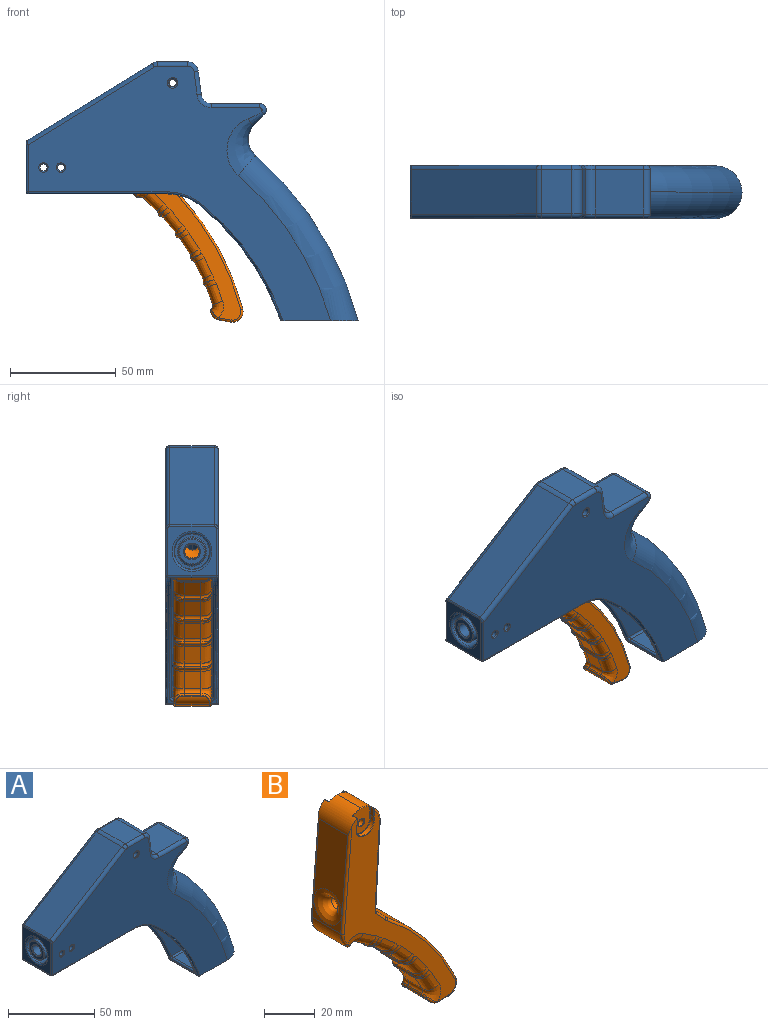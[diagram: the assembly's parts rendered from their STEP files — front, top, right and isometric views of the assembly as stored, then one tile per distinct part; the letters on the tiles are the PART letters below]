
ASSEMBLY  parts=2 mates=1
PART A: 167 faces, bbox 174.9x30.6x133.7 mm
  f0: cylinder r=3.5mm len=44.85mm, axis (-1,0,0), area 930.7mm2, adj f96,f97,f103,f104,f111,f113
  f1: cone r=6.35mm half-angle=0.3deg, axis (1,0,0), area 902mm2, adj f98,f99,f105,f106,f112,f114
  f2: cone r=8.3mm half-angle=0.3deg, axis (-1,0,0), area 1204.9mm2, adj f48,f70,f100,f101,f107,f108
  f3: plane 114.93x97.12mm, normal (0,1,0), area 3888.3mm2, adj f67,f68,f69,f80,f123,f129,f132,f136
  f4: plane 17.5x9.2mm, normal (0.52,0,-0.85), area 189.1mm2, adj f53,f140,f146,f149
  f5: plane 114.93x97.12mm, normal (0,-1,0), area 3888.3mm2, adj f64,f65,f66,f82,f115,f116,f120,f121
  f6: cylinder r=120mm len=53.62mm, axis (0,1,0), area 118.4mm2, adj f7,f15,f119,f121,f122,f126,f129,f161
  f7: cylinder r=25mm len=15.72mm, axis (0,1,0), area 12.8mm2, adj f6,f14,f125,f164
  f8: plane 21x11.13mm, normal (0.99,0,0.13), area 235.7mm2, adj f9,f21,f30,f43
  f9: cylinder r=5mm len=21mm, axis (0,1,0), area 151.3mm2, adj f8,f10,f29,f44
  f10: plane 21x14.2mm, normal (0,0,1), area 298.1mm2, adj f9,f11,f28,f45
  f11: cylinder r=5mm len=21mm, axis (0,1,0), area 58mm2, adj f10,f12,f27,f46
  f12: plane 59.18x36.47mm, normal (-0.52,0,0.85), area 1459.8mm2, adj f11,f26,f47,f75
  f13: plane 23.44x23mm, normal (-1,0,0), area 258.5mm2, adj f70,f71,f72,f73,f74,f75,f76
  f14: plane 65.73x23mm, normal (0,0,-1), area 1021.6mm2, adj f7,f15,f72,f128,f131,f135,f136,f139
  f15: cylinder r=25mm len=15.72mm, axis (0,1,0), area 12.8mm2, adj f6,f14,f132,f160
  f16: plane 37.37x26.55mm, normal (0,0,-1), area 826mm2, adj f22,f23,f36,f37,f161,f162,f163
  f17: cylinder r=10mm len=16.85mm, axis (0,1,0), area 138.3mm2, adj f18,f35,f38
  f18: plane 21.39x5.09mm, normal (0.71,0,-0.71), area 129.6mm2, adj f17,f19,f34,f39
  f19: cylinder r=3mm len=21mm, axis (0,1,0), area 148.4mm2, adj f18,f20,f33,f40
  f20: plane 22.76x21mm, normal (0,0,1), area 477.9mm2, adj f19,f21,f32,f41
  f21: cylinder r=5mm len=21mm, axis (0,1,0), area 151.3mm2, adj f8,f20,f31,f42
  f22: plane 143.42x120.75mm, normal (0,-1,0), area 5946.3mm2, adj f16,f37,f38,f39,f40,f41,f42,f43
  f23: plane 143.42x120.74mm, normal (0,1,0), area 5946.2mm2, adj f16,f26,f27,f28,f29,f30,f31,f32
  f24: cylinder r=2mm len=4.25mm, axis (0,-1,0), area 53.4mm2, adj f77,f84
  f25: cylinder r=2mm len=4.25mm, axis (0,1,0), area 53.4mm2, adj f78,f83
  f26: cylinder r=2mm len=60.75mm, axis (-0.85,0,-0.52), area 219.3mm2, adj f12,f23,f27,f73
  f27: torus R=3mm, axis (0,-1,0), area 7.4mm2, adj f11,f23,f26,f28
  f28: cylinder r=2mm len=14.2mm, axis (-1,0,0), area 44.6mm2, adj f10,f23,f27,f29
  f29: torus R=3mm, axis (0,-1,0), area 19.3mm2, adj f9,f23,f28,f30
  f30: cylinder r=2mm len=11.39mm, axis (-0.13,0,0.99), area 35.3mm2, adj f8,f23,f29,f31
  f31: torus R=7mm, axis (0,-1,0), area 25.9mm2, adj f21,f23,f30,f32
  f32: cylinder r=2mm len=22.76mm, axis (-1,0,0), area 71.5mm2, adj f20,f23,f31,f33
  f33: torus R=1mm, axis (0,-1,0), area 16.8mm2, adj f19,f23,f32,f34
  f34: bspline ~7.58x7.43mm, area 32.1mm2, adj f18,f23,f33,f35
  f35: bspline ~26.95x13.55mm, area 317.6mm2, adj f17,f23,f34,f36
  f36: torus R=142.5mm, axis (0,-1,0), area 1744.8mm2, adj f16,f23,f35,f37
  f37: torus R=142.5mm, axis (0,-1,0), area 1744.8mm2, adj f16,f22,f36,f38
  f38: bspline ~26.95x13.55mm, area 317.6mm2, adj f17,f22,f37,f39
  f39: bspline ~7.58x7.43mm, area 32.1mm2, adj f18,f22,f38,f40
  f40: torus R=1mm, axis (0,-1,0), area 16.8mm2, adj f19,f22,f39,f41
  f41: cylinder r=2mm len=22.76mm, axis (1,0,0), area 71.5mm2, adj f20,f22,f40,f42
  f42: torus R=7mm, axis (0,-1,0), area 25.9mm2, adj f21,f22,f41,f43
  f43: cylinder r=2mm len=11.39mm, axis (0.13,0,-0.99), area 35.3mm2, adj f8,f22,f42,f44
  f44: torus R=3mm, axis (0,-1,0), area 19.3mm2, adj f9,f22,f43,f45
  f45: cylinder r=2mm len=14.2mm, axis (1,0,0), area 44.6mm2, adj f10,f22,f44,f46
  f46: torus R=3mm, axis (0,-1,0), area 7.4mm2, adj f11,f22,f45,f47
  f47: cylinder r=2mm len=60.75mm, axis (0.85,0,0.52), area 219.3mm2, adj f12,f22,f46,f76
  f48: plane 16.6x16.6mm, normal (-1,0,0), area 62.6mm2, adj f2,f114
  f49: plane 11.71x11.71mm, normal (-1,0,0), area 57.4mm2, adj f112,f113
  f50: plane 17.5x11.13mm, normal (-0.99,0,-0.13), area 196.4mm2, adj f51,f59,f127,f153
  f51: cylinder r=2.25mm len=17.5mm, axis (0,1,0), area 56.7mm2, adj f50,f52,f130,f152
  f52: plane 17.5x14.2mm, normal (0,0,-1), area 248.4mm2, adj f51,f53,f133,f151
  f53: cylinder r=2.25mm len=17.5mm, axis (0,1,0), area 21.7mm2, adj f4,f52,f137,f150
  f54: plane 31.15x17.5mm, normal (0,0,1), area 510.8mm2, adj f116,f117,f122,f123
  f55: cylinder r=12.75mm len=18.65mm, axis (0,1,0), area 176.3mm2, adj f56,f65,f68
  f56: plane 17.54x4.74mm, normal (-0.71,0,0.71), area 116.1mm2, adj f55,f57,f64,f69,f115,f157
  f57: cylinder r=0.25mm len=17.5mm, axis (0,1,0), area 10.3mm2, adj f56,f58,f118,f156
  f58: plane 22.76x17.5mm, normal (0,0,-1), area 398.3mm2, adj f57,f59,f120,f155
  f59: cylinder r=7.75mm len=17.5mm, axis (0,1,0), area 195.4mm2, adj f50,f58,f124,f154
  f60: cylinder r=4.75mm len=9.5mm, axis (0,-1,0), area 44.8mm2, adj f80,f81
  f61: plane 8.5x8.5mm, normal (0,1,0), area 37.1mm2, adj f77,f81
  f62: cylinder r=4.75mm len=9.5mm, axis (0,1,0), area 44.8mm2, adj f79,f82
  f63: plane 8.5x8.5mm, normal (0,-1,0), area 37.1mm2, adj f78,f79
  f64: offset ~10.06x9.58mm, area 1.5mm2, adj f5,f56,f65,f115
  f65: offset ~32.45x19.05mm, area 253.4mm2, adj f5,f55,f64,f66
  f66: torus R=142.5mm, axis (0,-1,0), area 1277mm2, adj f5,f65,f67,f117
  f67: torus R=142.5mm, axis (0,-1,0), area 1277mm2, adj f3,f66,f68,f117
  f68: offset ~32.45x19.05mm, area 253.4mm2, adj f3,f55,f67,f69
  f69: offset ~10.06x9.58mm, area 1.5mm2, adj f3,f56,f68,f157
  f70: torus R=9.44mm, axis (1,0,0), area 86.6mm2, adj f2,f13
  f71: cylinder r=1mm len=22.27mm, axis (0,0,-1), area 35mm2, adj f13,f23,f73,f166
  f72: cylinder r=1mm len=23mm, axis (0,1,0), area 36.1mm2, adj f13,f14,f158,f166
  f73: bspline ~2.39x2.15mm, area 3.1mm2, adj f13,f26,f71,f75
  f74: cylinder r=1mm len=22.27mm, axis (0,0,1), area 35mm2, adj f13,f22,f76,f158
  f75: cylinder r=1mm len=21mm, axis (0,1,0), area 21.4mm2, adj f12,f13,f73,f76
  f76: bspline ~2.39x2.07mm, area 3.1mm2, adj f13,f47,f74,f75
  f77: torus R=2.5mm, axis (0,-1,0), area 10.8mm2, adj f24,f61
  f78: torus R=2.5mm, axis (0,1,0), area 10.8mm2, adj f25,f63
  f79: torus R=4.25mm, axis (0,1,0), area 22.5mm2, adj f62,f63
  f80: torus R=5.25mm, axis (0,-1,0), area 24.3mm2, adj f3,f60
  f81: torus R=4.25mm, axis (0,-1,0), area 22.5mm2, adj f60,f61
  f82: torus R=5.25mm, axis (0,-1,0), area 24.3mm2, adj f5,f62
  f83: torus R=2.5mm, axis (0,-1,0), area 10.8mm2, adj f23,f25
  f84: torus R=2.5mm, axis (0,-1,0), area 10.8mm2, adj f22,f24
  f85: plane 17.5x2.16mm, normal (1,0,0), area 37.8mm2, adj f141,f142,f146,f147
  f86: plane 49.74x17.5mm, normal (0.99,0,-0.13), area 827.3mm2, adj f111,f134,f135,f142,f143
  f87: cylinder r=1.7mm len=3.4mm, axis (0,1,0), area 35.9mm2, adj f108,f109
  f88: cylinder r=1.7mm len=3.4mm, axis (0,1,0), area 34.3mm2, adj f102,f107
  f89: cylinder r=1.7mm len=3.4mm, axis (0,1,0), area 35.3mm2, adj f101,f110
  f90: cylinder r=1.7mm len=3.4mm, axis (0,1,0), area 33.8mm2, adj f95,f100
  f91: cylinder r=1.7mm len=3.4mm, axis (0,1,0), area 24.3mm2, adj f104,f106
  f92: cylinder r=1.7mm len=3.4mm, axis (0,1,0), area 23mm2, adj f103,f105
  f93: cylinder r=1.7mm len=3.4mm, axis (0,1,0), area 23.7mm2, adj f97,f99
  f94: cylinder r=1.7mm len=3.4mm, axis (0,1,0), area 22.5mm2, adj f96,f98
  f95: torus R=2.2mm, axis (0,-1,0), area 9.3mm2, adj f22,f90
  f96: bspline ~4.41x3.85mm, area 7.5mm2, adj f0,f94
  f97: bspline ~4.41x3.85mm, area 7.5mm2, adj f0,f93
  f98: bspline ~4.77x4.41mm, area 10.7mm2, adj f1,f94
  f99: bspline ~4.78x4.4mm, area 10.7mm2, adj f1,f93
  f100: bspline ~4.41x4.16mm, area 8.5mm2, adj f2,f90
  f101: bspline ~4.41x4.16mm, area 8.5mm2, adj f2,f89
  f102: torus R=2.2mm, axis (0,-1,0), area 9.3mm2, adj f22,f88
  f103: bspline ~4.41x3.85mm, area 7.5mm2, adj f0,f92
  f104: bspline ~4.41x3.85mm, area 7.5mm2, adj f0,f91
  f105: bspline ~4.77x4.41mm, area 10.7mm2, adj f1,f92
  f106: bspline ~4.78x4.4mm, area 10.7mm2, adj f1,f91
  f107: bspline ~4.41x4.16mm, area 8.5mm2, adj f2,f88
  f108: bspline ~4.41x4.15mm, area 8.5mm2, adj f2,f87
  f109: torus R=2.2mm, axis (0,-1,0), area 9.3mm2, adj f23,f87
  f110: torus R=2.2mm, axis (0,-1,0), area 9.3mm2, adj f23,f89
  f111: bspline ~8x8mm, area 18.3mm2, adj f0,f86
  f112: torus R=5.85mm, axis (1,0,0), area 30.3mm2, adj f1,f49
  f113: torus R=4mm, axis (1,0,0), area 18.2mm2, adj f0,f49
  f114: torus R=7mm, axis (-1,0,0), area 32.8mm2, adj f1,f48
  f115: cylinder r=1mm len=4.92mm, axis (0.71,0,0.71), area 7.9mm2, adj f5,f56,f64,f118
  f116: cylinder r=1mm len=22.74mm, axis (-1,0,0), area 35.1mm2, adj f5,f54,f117,f119
  f117: bspline ~19.52x11.67mm, area 53mm2, adj f54,f66,f67,f116,f123
  f118: bspline ~2.41x1.31mm, area 0.5mm2, adj f57,f115,f120
  f119: bspline ~2.46x2.42mm, area 3.9mm2, adj f6,f116,f121,f122
  f120: cylinder r=1mm len=22.76mm, axis (1,0,0), area 34.3mm2, adj f5,f58,f118,f124
  f121: torus R=121mm, axis (0,-1,0), area 100.1mm2, adj f5,f6,f119,f125
  f122: cylinder r=1mm len=17.5mm, axis (0,1,0), area 33.5mm2, adj f6,f54,f119,f126
  f123: cylinder r=1mm len=22.74mm, axis (1,0,0), area 35.1mm2, adj f3,f54,f117,f126
  f124: torus R=8.75mm, axis (0,-1,0), area 18.4mm2, adj f5,f59,f120,f127
  f125: torus R=26mm, axis (0,-1,0), area 27.1mm2, adj f5,f7,f121,f128
  f126: bspline ~2.58x2.12mm, area 3.9mm2, adj f6,f122,f123,f129
  f127: cylinder r=1mm len=11.26mm, axis (0.13,0,-0.99), area 17.6mm2, adj f5,f50,f124,f130
  f128: cylinder r=1mm len=20.86mm, axis (1,0,0), area 32.8mm2, adj f5,f14,f125,f131
  f129: torus R=121mm, axis (0,-1,0), area 100.1mm2, adj f3,f6,f126,f132
  f130: torus R=1.25mm, axis (0,-1,0), area 4.3mm2, adj f5,f51,f127,f133
  f131: bspline ~2.51x2.02mm, area 3.3mm2, adj f14,f128,f134,f135
  f132: torus R=26mm, axis (0,-1,0), area 27.1mm2, adj f3,f15,f129,f136
  f133: cylinder r=1mm len=14.2mm, axis (1,0,0), area 22.3mm2, adj f5,f52,f130,f137
  f134: cylinder r=1mm len=49.87mm, axis (-0.13,0,-0.99), area 78.6mm2, adj f5,f86,f131,f138
  f135: cylinder r=1mm len=17.5mm, axis (0,-1,0), area 25.2mm2, adj f14,f86,f131,f139
  f136: cylinder r=1mm len=20.86mm, axis (-1,0,0), area 32.8mm2, adj f3,f14,f132,f139
  f137: torus R=1.25mm, axis (0,-1,0), area 1.6mm2, adj f5,f53,f133,f140
  f138: torus R=2mm, axis (0,-1,0), area 0.3mm2, adj f5,f134,f141,f142
  f139: bspline ~2.02x2mm, area 3.3mm2, adj f14,f135,f136,f143
  f140: cylinder r=1mm len=9.72mm, axis (0.85,0,0.52), area 17mm2, adj f4,f5,f137,f144
  f141: cylinder r=1mm len=2.16mm, axis (0,0,-1), area 3.4mm2, adj f5,f85,f138,f144
  f142: cylinder r=1mm len=17.5mm, axis (0,1,0), area 2.3mm2, adj f85,f86,f138,f145
  f143: cylinder r=1mm len=49.87mm, axis (-0.13,0,-0.99), area 78.6mm2, adj f3,f86,f139,f145
  f144: sphere r=1mm, area 0.7mm2, adj f140,f141,f146
  f145: torus R=2mm, axis (0,-1,0), area 0.3mm2, adj f3,f142,f143,f147
  f146: cylinder r=1mm len=17.5mm, axis (0,1,0), area 17.8mm2, adj f4,f85,f144,f148
  f147: cylinder r=1mm len=2.16mm, axis (0,0,1), area 3.4mm2, adj f3,f85,f145,f148
  f148: sphere r=1mm, area 0.7mm2, adj f146,f147,f149
  f149: cylinder r=1mm len=9.72mm, axis (0.85,0,0.52), area 17mm2, adj f3,f4,f148,f150
  f150: torus R=1.25mm, axis (0,-1,0), area 1.6mm2, adj f3,f53,f149,f151
  f151: cylinder r=1mm len=14.2mm, axis (1,0,0), area 22.3mm2, adj f3,f52,f150,f152
  f152: torus R=1.25mm, axis (0,-1,0), area 4.3mm2, adj f3,f51,f151,f153
  f153: cylinder r=1mm len=11.26mm, axis (0.13,0,-0.99), area 17.6mm2, adj f3,f50,f152,f154
  f154: torus R=8.75mm, axis (0,-1,0), area 18.4mm2, adj f3,f59,f153,f155
  f155: cylinder r=1mm len=22.76mm, axis (1,0,0), area 34.3mm2, adj f3,f58,f154,f156
  f156: bspline ~2.41x1.31mm, area 0.5mm2, adj f57,f155,f157
  f157: cylinder r=1mm len=4.92mm, axis (-0.71,0,-0.71), area 7.9mm2, adj f3,f56,f69,f156
  f158: sphere r=1mm, area 1.6mm2, adj f72,f74,f159
  f159: cylinder r=1mm len=65.73mm, axis (-1,0,0), area 103.2mm2, adj f14,f22,f158,f160
  f160: torus R=26mm, axis (0,-1,0), area 27.1mm2, adj f15,f22,f159,f161
  f161: torus R=121mm, axis (0,-1,0), area 105.6mm2, adj f6,f16,f22,f160,f162
  f162: cylinder r=1mm len=24.89mm, axis (0,1,0), area 29.5mm2, adj f6,f16,f161,f163
  f163: torus R=121mm, axis (0,-1,0), area 105.6mm2, adj f6,f16,f23,f162,f164
  f164: torus R=26mm, axis (0,-1,0), area 27.1mm2, adj f7,f23,f163,f165
  f165: cylinder r=1mm len=65.73mm, axis (1,0,0), area 103.2mm2, adj f14,f23,f164,f166
  f166: sphere r=1mm, area 2.1mm2, adj f71,f72,f165
PART B: 147 faces, bbox 74.2x18.1x114.9 mm
  f0: cylinder r=109.84mm len=12.17mm, axis (0,1,0), area 3.5mm2, adj f13,f72,f73,f74
  f1: cylinder r=9mm len=16mm, axis (0,1,0), area 216mm2, adj f2,f21,f79,f85,f119,f121,f122,f131
  f2: cylinder r=9mm len=18mm, axis (0,1,0), area 209.7mm2, adj f1,f12,f22,f23,f69,f77,f114,f115
  f3: cylinder r=1.65mm len=13.08mm, axis (0,1,0), area 135.6mm2, adj f137,f138
  f4: plane 11.58x9.66mm, normal (0,-1,0), area 83.5mm2, adj f126,f128,f129,f130,f131,f138
  f5: plane 11.58x9.66mm, normal (0,1,0), area 83.5mm2, adj f116,f117,f118,f119,f120,f137
  f6: plane 3.73x1.83mm, normal (-1,0,0.06), area 6.7mm2, adj f8,f130,f134,f135,f136
  f7: plane 3.69x2.14mm, normal (1,0,-0.06), area 7.3mm2, adj f8,f22,f125,f126,f132
  f8: cylinder r=5mm len=10mm, axis (0,1,0), area 34.3mm2, adj f6,f7,f128,f132
  f9: plane 3.73x1.83mm, normal (-1,0,0.06), area 6.7mm2, adj f10,f120,f122,f123,f124
  f10: cylinder r=5mm len=10mm, axis (0,1,0), area 38.1mm2, adj f9,f11,f23,f118,f124
  f11: plane 3.59x2.04mm, normal (1,0,-0.06), area 7.3mm2, adj f10,f23,f114,f116
  f12: plane 45.59x16mm, normal (-1,0,0.09), area 543.3mm2, adj f2,f13,f69,f77,f141
  f13: cylinder r=10mm len=16mm, axis (0,1,0), area 169.5mm2, adj f0,f12,f70,f71,f75,f76
  f14: cylinder r=109.84mm len=12.17mm, axis (0,1,0), area 3.5mm2, adj f15,f93,f95,f97
  f15: cylinder r=5mm len=16mm, axis (0,1,0), area 85.7mm2, adj f14,f16,f89,f91,f99,f101
  f16: plane 16x5.52mm, normal (0,0,-1), area 88.3mm2, adj f15,f17,f86,f100
  f17: cylinder r=5mm len=16mm, axis (0,1,0), area 159.9mm2, adj f16,f18,f83,f98
  f18: cylinder r=124.84mm len=47.62mm, axis (0,1,0), area 985.7mm2, adj f17,f19,f80,f96
  f19: cylinder r=10mm len=16mm, axis (0,1,0), area 26.7mm2, adj f18,f20,f78,f94
  f20: plane 16x5.48mm, normal (0.73,0,0.69), area 120.5mm2, adj f19,f81,f87,f92
  f21: plane 42.05x16mm, normal (1,0,-0.06), area 581.1mm2, adj f1,f82,f87,f88,f143
  f22: plane 111.21x62.41mm, normal (0,-1,0), area 1349.9mm2, adj f2,f7,f54,f55,f56,f57,f58,f59
  f23: plane 111.21x62.41mm, normal (0,1,0), area 1353.9mm2, adj f2,f10,f11,f39,f40,f41,f42,f43
  f24: cylinder r=2mm len=8mm, axis (0,-1,0), area 20mm2, adj f25,f53,f68,f95
  f25: plane 8x7.62mm, normal (-0.87,0,-0.49), area 70.1mm2, adj f24,f26,f52,f67
  f26: cylinder r=2mm len=8mm, axis (0,-1,0), area 12.6mm2, adj f25,f51,f66,f113
  f27: plane 8x7.28mm, normal (-0.56,0,-0.83), area 70.1mm2, adj f28,f29,f40,f55
  f28: cylinder r=2mm len=8mm, axis (0,-1,0), area 20mm2, adj f27,f39,f54,f73
  f29: cylinder r=2mm len=8mm, axis (0,-1,0), area 12.6mm2, adj f27,f41,f56,f103
  f30: cylinder r=2mm len=8mm, axis (0,-1,0), area 12.6mm2, adj f31,f47,f62,f106
  f31: plane 8x6.42mm, normal (-0.73,0,-0.68), area 70.1mm2, adj f30,f32,f46,f61
  f32: cylinder r=2mm len=8mm, axis (0,-1,0), area 12.6mm2, adj f31,f45,f60,f110
  f33: plane 8x6.67mm, normal (-0.65,0,-0.76), area 70.1mm2, adj f34,f35,f43,f58
  f34: cylinder r=2mm len=8mm, axis (0,-1,0), area 12.6mm2, adj f33,f42,f57,f103
  f35: cylinder r=2mm len=8mm, axis (0,-1,0), area 12.6mm2, adj f33,f44,f59,f110
  f36: cylinder r=2mm len=8mm, axis (0,-1,0), area 12.6mm2, adj f37,f50,f65,f113
  f37: plane 8x7.06mm, normal (-0.81,0,-0.59), area 70.1mm2, adj f36,f38,f49,f64
  f38: cylinder r=2mm len=8mm, axis (0,-1,0), area 12.6mm2, adj f37,f48,f63,f106
  f39: bspline ~8.79x5.57mm, area 39.7mm2, adj f23,f28,f40,f74,f75
  f40: bspline ~10.06x9.02mm, area 71.2mm2, adj f23,f27,f39,f41
  f41: bspline ~5.76x5.44mm, area 15.6mm2, adj f23,f29,f40,f104
  f42: bspline ~5.48x5.12mm, area 15.6mm2, adj f23,f34,f43,f104
  f43: bspline ~9.91x9.49mm, area 71.2mm2, adj f23,f33,f42,f44
  f44: bspline ~9.19x5.91mm, area 15.6mm2, adj f23,f35,f43,f108
  f45: bspline ~9.24x5.77mm, area 15.6mm2, adj f23,f32,f46,f108
  f46: bspline ~9.82x9.63mm, area 71.2mm2, adj f23,f31,f45,f47
  f47: bspline ~9.3x5.63mm, area 15.6mm2, adj f23,f30,f46,f107
  f48: bspline ~9.05x6.11mm, area 15.6mm2, adj f23,f38,f49,f107
  f49: bspline ~10.02x9.21mm, area 71.2mm2, adj f23,f37,f48,f50
  f50: bspline ~9.28x5.75mm, area 15.6mm2, adj f23,f36,f49,f111
  f51: bspline ~8.74x6.37mm, area 15.6mm2, adj f23,f26,f52,f111
  f52: bspline ~10.09x8.67mm, area 71.2mm2, adj f23,f25,f51,f53
  f53: bspline ~8.33x5.56mm, area 37.7mm2, adj f23,f24,f52,f97,f99
  f54: bspline ~8.79x5.57mm, area 39.7mm2, adj f22,f28,f55,f71,f72
  f55: bspline ~10.06x9.02mm, area 71.2mm2, adj f22,f27,f54,f56
  f56: bspline ~5.76x5.44mm, area 15.6mm2, adj f22,f29,f55,f102
  f57: bspline ~9.31x5.61mm, area 15.6mm2, adj f22,f34,f58,f102
  f58: bspline ~9.91x9.49mm, area 71.2mm2, adj f22,f33,f57,f59
  f59: bspline ~9.19x5.91mm, area 15.6mm2, adj f22,f35,f58,f109
  f60: bspline ~9.24x5.77mm, area 15.6mm2, adj f22,f32,f61,f109
  f61: bspline ~9.82x9.63mm, area 71.2mm2, adj f22,f31,f60,f62
  f62: bspline ~9.3x5.63mm, area 15.6mm2, adj f22,f30,f61,f105
  f63: bspline ~9.05x6.11mm, area 15.6mm2, adj f22,f38,f64,f105
  f64: bspline ~10.02x9.21mm, area 71.2mm2, adj f22,f37,f63,f65
  f65: bspline ~9.28x5.75mm, area 15.6mm2, adj f22,f36,f64,f112
  f66: bspline ~8.74x6.37mm, area 15.6mm2, adj f22,f26,f67,f112
  f67: bspline ~10.09x8.67mm, area 71.2mm2, adj f22,f25,f66,f68
  f68: bspline ~8.33x5.56mm, area 37.7mm2, adj f22,f24,f67,f91,f93
  f69: cylinder r=1mm len=49.78mm, axis (-0.09,0,-1), area 75.1mm2, adj f2,f12,f22,f70
  f70: torus R=9mm, axis (0,-1,0), area 10.5mm2, adj f13,f22,f69,f71
  f71: bspline ~5.05x4.63mm, area 8mm2, adj f13,f54,f70,f72
  f72: bspline ~5.21x1.7mm, area 2.8mm2, adj f0,f54,f71,f73
  f73: cylinder r=1mm len=8mm, axis (0,-1,0), area 9.5mm2, adj f0,f28,f72,f74
  f74: bspline ~5.21x1.7mm, area 2.8mm2, adj f0,f39,f73,f75
  f75: bspline ~4.82x4.52mm, area 8mm2, adj f13,f39,f74,f76
  f76: torus R=9mm, axis (0,-1,0), area 10.5mm2, adj f13,f23,f75,f77
  f77: cylinder r=1mm len=49.78mm, axis (0.09,0,1), area 75.1mm2, adj f2,f12,f23,f76
  f78: torus R=11mm, axis (0,-1,0), area 2.7mm2, adj f19,f22,f80,f81
  f79: torus R=8mm, axis (0,-1,0), area 12.7mm2, adj f1,f22,f82,f136
  f80: torus R=123.84mm, axis (0,-1,0), area 96.5mm2, adj f18,f22,f78,f83
  f81: cylinder r=1mm len=6.17mm, axis (0.69,0,-0.73), area 11.8mm2, adj f20,f22,f78,f84
  f82: cylinder r=1mm len=42.11mm, axis (-0.06,0,-1), area 66.2mm2, adj f21,f22,f79,f84
  f83: torus R=4mm, axis (0,-1,0), area 14.6mm2, adj f17,f22,f80,f86
  f84: torus R=2mm, axis (0,-1,0), area 1.7mm2, adj f22,f81,f82,f87
  f85: torus R=8mm, axis (0,-1,0), area 12.7mm2, adj f1,f23,f88,f123
  f86: cylinder r=1mm len=5.52mm, axis (-1,0,0), area 8.7mm2, adj f16,f22,f83,f89
  f87: cylinder r=1mm len=16mm, axis (0,-1,0), area 12.7mm2, adj f20,f21,f84,f90,f144
  f88: cylinder r=1mm len=42.11mm, axis (0.06,0,1), area 66.2mm2, adj f21,f23,f85,f90
  f89: torus R=4mm, axis (0,-1,0), area 1.2mm2, adj f15,f22,f86,f91
  f90: torus R=2mm, axis (0,-1,0), area 1.7mm2, adj f23,f87,f88,f92
  f91: bspline ~5.25x3.97mm, area 8.9mm2, adj f15,f68,f89,f93
  f92: cylinder r=1mm len=6.17mm, axis (-0.69,0,0.73), area 11.8mm2, adj f20,f23,f90,f94
  f93: bspline ~5.21x1.71mm, area 2.8mm2, adj f14,f68,f91,f95
  f94: torus R=11mm, axis (0,-1,0), area 2.7mm2, adj f19,f23,f92,f96
  f95: cylinder r=1mm len=8mm, axis (0,-1,0), area 9.5mm2, adj f14,f24,f93,f97
  f96: torus R=123.84mm, axis (0,-1,0), area 96.5mm2, adj f18,f23,f94,f98
  f97: bspline ~5.21x1.71mm, area 2.8mm2, adj f14,f53,f95,f99
  f98: torus R=4mm, axis (0,-1,0), area 14.6mm2, adj f17,f23,f96,f100
  f99: bspline ~5.29x4.1mm, area 8.9mm2, adj f15,f53,f97,f101
  f100: cylinder r=1mm len=5.52mm, axis (1,0,0), area 8.7mm2, adj f16,f23,f98,f101
  f101: torus R=4mm, axis (0,-1,0), area 1.2mm2, adj f15,f23,f99,f100
  f102: bspline ~5.49x4.64mm, area 4.4mm2, adj f56,f57,f103
  f103: cylinder r=1mm len=8mm, axis (0,-1,0), area 11.7mm2, adj f29,f34,f102,f104
  f104: bspline ~5x4.64mm, area 4.4mm2, adj f41,f42,f103
  f105: bspline ~6.95x4.48mm, area 4.4mm2, adj f62,f63,f106
  f106: cylinder r=1mm len=8mm, axis (0,-1,0), area 11.7mm2, adj f30,f38,f105,f107
  f107: bspline ~5.49x4.48mm, area 4.4mm2, adj f47,f48,f106
  f108: bspline ~6.95x4.23mm, area 4.4mm2, adj f44,f45,f110
  f109: bspline ~5.49x4.23mm, area 4.4mm2, adj f59,f60,f110
  f110: cylinder r=1mm len=8mm, axis (0,-1,0), area 11.7mm2, adj f32,f35,f108,f109
  f111: bspline ~6.95x4.88mm, area 4.4mm2, adj f50,f51,f113
  f112: bspline ~5x4.88mm, area 4.4mm2, adj f65,f66,f113
  f113: cylinder r=1mm len=8mm, axis (0,-1,0), area 11.7mm2, adj f26,f36,f111,f112
  f114: cylinder r=0.21mm len=2.04mm, axis (0,1,0), area 0.9mm2, adj f2,f11,f23,f115
  f115: bspline ~0.57x0.49mm, area 0.2mm2, adj f2,f114,f116,f117
  f116: cylinder r=0.21mm len=3.92mm, axis (-0.06,0,-1), area 1.2mm2, adj f5,f11,f115,f118
  f117: torus R=8.79mm, axis (0,-1,0), area 1.5mm2, adj f2,f5,f115,f119
  f118: torus R=4.79mm, axis (0,-1,0), area 6.1mm2, adj f5,f10,f116,f120
  f119: torus R=8.79mm, axis (0,-1,0), area 1.7mm2, adj f1,f5,f117,f121
  f120: cylinder r=0.21mm len=4.05mm, axis (0.06,0,1), area 1.3mm2, adj f5,f9,f118,f121
  f121: bspline ~0.58x0.52mm, area 0.2mm2, adj f1,f119,f120,f122
  f122: cylinder r=0.21mm len=1.04mm, axis (0,1,0), area 0.5mm2, adj f1,f9,f121,f123
  f123: bspline ~1.47x1.26mm, area 0.7mm2, adj f9,f85,f122,f124
  f124: cylinder r=0.21mm len=3.81mm, axis (-0.06,0,-1), area 1.1mm2, adj f9,f10,f23,f123
  f125: cylinder r=0.21mm len=2.04mm, axis (0,1,0), area 0.9mm2, adj f2,f7,f22,f127
  f126: cylinder r=0.21mm len=3.92mm, axis (0.06,0,1), area 1.2mm2, adj f4,f7,f127,f128
  f127: bspline ~0.6x0.52mm, area 0.2mm2, adj f2,f125,f126,f129
  f128: torus R=4.79mm, axis (0,-1,0), area 6.1mm2, adj f4,f8,f126,f130
  f129: torus R=8.79mm, axis (0,-1,0), area 1.5mm2, adj f2,f4,f127,f131
  f130: cylinder r=0.21mm len=4.05mm, axis (-0.06,0,-1), area 1.3mm2, adj f4,f6,f128,f133
  f131: torus R=8.79mm, axis (0,-1,0), area 1.7mm2, adj f1,f4,f129,f133
  f132: torus R=5.21mm, axis (0,-1,0), area 6.4mm2, adj f7,f8,f22,f134
  f133: bspline ~0.55x0.49mm, area 0.2mm2, adj f1,f130,f131,f135
  f134: cylinder r=0.21mm len=2.77mm, axis (0.06,0,1), area 0.9mm2, adj f6,f22,f132,f136
  f135: cylinder r=0.21mm len=1.04mm, axis (0,1,0), area 0.5mm2, adj f1,f6,f133,f136
  f136: bspline ~1.7x1.08mm, area 0.7mm2, adj f6,f79,f134,f135
  f137: torus R=1.86mm, axis (0,-1,0), area 3.6mm2, adj f3,f5
  f138: torus R=1.86mm, axis (0,-1,0), area 3.6mm2, adj f3,f4
  f139: cylinder r=2.75mm len=8.78mm, axis (1,0,-0.06), area 142.9mm2, adj f141,f145
  f140: plane 8.77x8.75mm, normal (1,0,-0.06), area 27.2mm2, adj f145,f146
  f141: bspline ~15.49x15.43mm, area 225.4mm2, adj f12,f139
  f142: cone r=4.88mm half-angle=1deg, axis (1,0,-0.06), area 124.2mm2, adj f143,f144,f146
  f143: torus R=5.45mm, axis (1,0,-0.06), area 22.7mm2, adj f21,f142,f144
  f144: bspline ~3.58x0.74mm, area 2.2mm2, adj f87,f142,f143
  f145: torus R=3.25mm, axis (1,0,-0.06), area 14.5mm2, adj f139,f140
  f146: torus R=4.38mm, axis (1,0,-0.06), area 22.9mm2, adj f140,f142
PLACE A t=(-17.44,-0.16,-0.93)mm fixed
PLACE B rot(axis=(0,1,0),10deg) t=(-22.69,-0.41,11.9)mm
MATE revolute B.f3 <-> A.f24  axis (0,-1,0) through (53.22,-7.16,35.46)mm
